# Revit family: Haworth_Cappellini_Mush_SideTable_AP_PRELIMINARY
name_source: partatom
category: Furniture
revit_build: Autodesk Revit 2018 (Build: 20170223_1515(x64)
units: mm (PartAtom-declared; Revit-internal decimal feet)

## family parameters
Always vertical = Yes
Cut with Voids When Loaded = No
OmniClass Number = 23.40.20.00
OmniClass Title = General Furniture and Specialties
Room Calculation Point = No
Shared = No
Work Plane-Based = No

## types (4) — shared parameters
Actual Depth = 500 mm  [stored 1.64042 ft]
Actual Diameter = 250 mm  [stored 0.82021 ft]
Actual Width = 500 mm  [stored 1.64042 ft]
Assembly Code = E2020200
Base Finish = Haworth _ Paint _ Undecided _ Table
Description = Haworth - Cappellini - Mush - Side Table
Manufacturer = Haworth
Max. Height = 470 mm  [stored 1.54199 ft]
Min. Height = 310 mm  [stored 1.01706 ft]
Model = MU_XX
Size = Verify Final Dim. w/ Haworth
Standard Height = 310, 320, 460, 470mm
URL = https://www.haworth.com
URL - Product = https://www.haworth.com
Version = 1
Warranty = http://www.haworth.com

## per-type parameters (varying)
| type | Actual Height | Height | Thickness | Under Surface |
| MU_2M | 460 mm  [stored 1.50919 ft] | 460 mm  [stored 1.50919 ft] | 4 mm  [stored 0.0131234 ft] | No |
| MU_2R | 470 mm  [stored 1.54199 ft] | 470 mm  [stored 1.54199 ft] | 12 mm  [stored 0.0393701 ft] | Yes |
| MU_1R | 320 mm  [stored 1.04987 ft] | 320 mm  [stored 1.04987 ft] | 12 mm  [stored 0.0393701 ft] | Yes |
| MU_1M | 310 mm  [stored 1.01706 ft] | 310 mm  [stored 1.01706 ft] | 4 mm  [stored 0.0131234 ft] | No |

note: [stored X ft] marks values corroborated as IEEE doubles in the binary element streams (Revit-internal decimal feet)

## geometry (parser evidence)
native form markers: Sweep x1
no freeform markers — native parametric forms only
